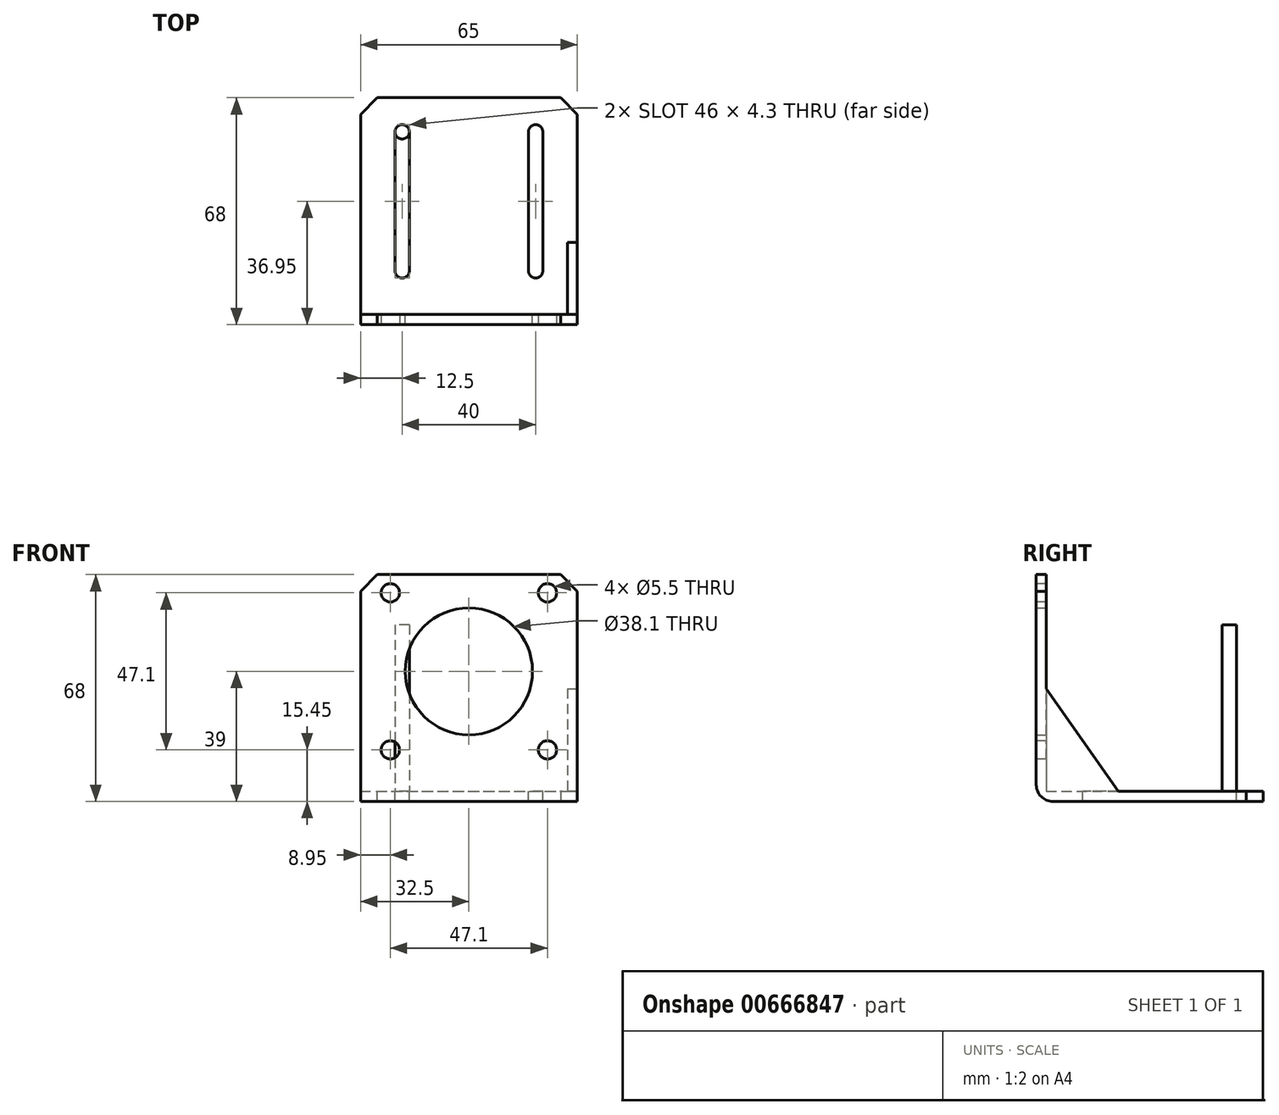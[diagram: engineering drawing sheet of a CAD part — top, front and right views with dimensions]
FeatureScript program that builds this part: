
annotation { "Feature Type Name" : "Feature", "Feature Type Description" : "" }
export const myFeature = defineFeature(function(context is Context, id is Id, definition is map)
    precondition{}
    {
        {
            var Q0;
            Q0=qCreatedBy(makeId("Top.planeOp"),FACE);
            var sketch = newSketch(context, id + "F0", { "sketchPlane" : qUnion([Q0])});
            skLineSegment(sketch, "E0.bottom", {"start": v(0, 0) * mm, "end": v(65, 0) * mm});
            skLineSegment(sketch, "E0.top", {"start": v(0, 65) * mm, "end": v(65, 65) * mm});
            skLineSegment(sketch, "E0.left", {"start": v(0, 0) * mm, "end": v(0, 65) * mm});
            skLineSegment(sketch, "E0.right", {"start": v(65, 0) * mm, "end": v(65, 65) * mm});
            skLineSegment(sketch, "E1.top", {"start": v(0, -3) * mm, "end": v(65, -3) * mm});
            skLineSegment(sketch, "E1.left", {"start": v(0, 0) * mm, "end": v(0, -3) * mm});
            skLineSegment(sketch, "E1.right", {"start": v(65, 0) * mm, "end": v(65, -3) * mm});
            skSolve(sketch);
        }
        {
            var Q0;
            Q0=makeQuery(id+"F0.imprint","IMPRINT",FACE,{"disambiguationData":[TD([[makeQuery(id+"F0.imprint","IMPRINT",EDGE,{"derivedFrom":sQuery(id+"F0.wireOp",EDGE,"E0.top")}),-1.0]])]});
            extrude(context, id + "F1", {"entities" : qUnion([Q0]), "depth" : 3 * mm, "offsetDistance" : 25 * mm});
        }
        {
            var Q0;
            Q0=makeQuery(id+"F0.imprint","IMPRINT",FACE,{"disambiguationData":[TD([[makeQuery(id+"F0.imprint","IMPRINT",EDGE,{"derivedFrom":sQuery(id+"F0.wireOp",EDGE,"E0.bottom")}),-1.0]])]});
            extrude(context, id + "F2", {"entities" : qUnion([Q0]), "operationType" : NewBodyOperationType.ADD, "depth" : 68 * mm, "offsetDistance" : 25 * mm});
        }
        {
            var Q0;
            Q0=makeQuery(id+"F2.opExtrude","CAP_EDGE",EDGE,{"disambiguationData":[OSD([sQuery(id+"F0.wireOp",EDGE,"E1.top")])],"isStart":true});
            fillet(context, id + "F3", {"entities" : qUnion([Q0]), "radius" : 5 * mm, "tangentPropagation" : true, "allowEdgeOverflow" : false});
        }
        {
            var Q0;
            Q0=makeQuery(id+"F2.opExtrude","CAP_EDGE",EDGE,{"disambiguationData":[OSD([sQuery(id+"F0.wireOp",EDGE,"E1.right")])],"isStart":false});
            var Q1;
            Q1=makeQuery(id+"F2.opExtrude","CAP_EDGE",EDGE,{"disambiguationData":[OSD([sQuery(id+"F0.wireOp",EDGE,"E1.left")])],"isStart":false});
            chamfer(context, id + "F4", {"entities" : qUnion([Q0, Q1]), "width" : 5 * mm, "tangentPropagation" : true});
        }
        {
            var Q0;
            Q0=makeQuery(id+"F2.opExtrude","SWEPT_FACE",FACE,{"disambiguationData":[OSD([sQuery(id+"F0.wireOp",EDGE,"E0.bottom")])]});
            var sketch = newSketch(context, id + "F5", { "sketchPlane" : qUnion([Q0])});
            skCircle(sketch, "E2", {"center": v(-32.5, 39) * mm, "radius": 19.05 * mm});
            skLineSegment(sketch, "E3.bottom", {"start": v(-8.95, 62.55) * mm, "end": v(-56.05, 62.55) * mm, "construction": true});
            skLineSegment(sketch, "E3.top", {"start": v(-8.95, 15.45) * mm, "end": v(-56.05, 15.45) * mm, "construction": true});
            skLineSegment(sketch, "E3.left", {"start": v(-8.95, 62.55) * mm, "end": v(-8.95, 15.45) * mm, "construction": true});
            skLineSegment(sketch, "E3.right", {"start": v(-56.05, 62.55) * mm, "end": v(-56.05, 15.45) * mm, "construction": true});
            skLineSegment(sketch, "E4", {"start": v(-32.5, 39) * mm, "end": v(-32.5, 68) * mm, "construction": true});
            skLineSegment(sketch, "E5", {"start": v(-65, 39) * mm, "end": v(-32.5, 39) * mm, "construction": true});
            skPoint(sketch, "E5.startSnap0", {"position": v(-56.05, 39) * mm});
            skLineSegment(sketch, "E6", {"start": v(-32.5, 39) * mm, "end": v(0, 39) * mm, "construction": true});
            skSolve(sketch);
        }
        {
            var Q0;
            Q0=sQuery(id+"F5.wireOp",VERTEX,"E3.bottom.end");
            var Q1;
            Q1=sQuery(id+"F5.wireOp",VERTEX,"E3.bottom.start");
            var Q2;
            Q2=sQuery(id+"F5.wireOp",VERTEX,"E3.top.start");
            var Q3;
            Q3=sQuery(id+"F5.wireOp",VERTEX,"E3.top.end");
            var Q4;
            Q4=makeQuery(id+"F1.opExtrude","SWEPT_BODY",BODY,{"disambiguationData":[OSD([sQuery(id+"F0.wireOp",EDGE,"E0.top"),sQuery(id+"F0.wireOp",EDGE,"E0.left"),sQuery(id+"F0.wireOp",EDGE,"E0.right"),sQuery(id+"F0.wireOp",EDGE,"E0.bottom")])]});
            hole(context, id + "F6", {"style" : HoleStyle.SIMPLE, "endStyle" : HoleEndStyle.THROUGH, "holeDiameter" : 5.5 * mm, "majorDiameter" : 5 * mm, "isTappedThrough" : true, "tappedDepth" : 12 * mm, "tapClearance" : 3, "locations" : qUnion([Q0, Q1, Q2, Q3]), "scope" : qUnion([Q4])});
        }
        {
            var Q0;
            Q0=makeQuery(id+"F5.imprint","IMPRINT",FACE,{"disambiguationData":[TD([[makeQuery(id+"F5.imprint","IMPRINT",EDGE,{"derivedFrom":sQuery(id+"F5.wireOp",EDGE,"E2")}),1.0]])]});
            extrude(context, id + "F7", {"entities" : qUnion([Q0]), "operationType" : NewBodyOperationType.REMOVE, "oppositeDirection" : true, "depth" : 25 * mm, "offsetDistance" : 25 * mm});
        }
        {
            var Q0;
            Q0=makeQuery(id+"F2.boolean.opBoolean","MERGE",FACE,{"derivedFrom":[makeQuery(id+"F1.opExtrude","SWEPT_FACE",FACE,{"disambiguationData":[OSD([sQuery(id+"F0.wireOp",EDGE,"E0.right")])]}),makeQuery(id+"F2.opExtrude","SWEPT_FACE",FACE,{"disambiguationData":[OSD([sQuery(id+"F0.wireOp",EDGE,"E1.right")])]})]});
            var sketch = newSketch(context, id + "F8", { "sketchPlane" : qUnion([Q0])});
            skLineSegment(sketch, "E7", {"start": v(0, 33.83) * mm, "end": v(21.59, 3) * mm});
            skSolve(sketch);
        }
        {
            var Q0;
            Q0 = qSketchRegion(id + "F8", true);
            var Q1;
            {var subQ0=sQuery(id+"F8.wireOp",EDGE,"E7");Q1=makeQuery(id+"F8.imprint","IMPRINT",FACE,{"disambiguationData":[TD([[makeQuery(id+"F8.imprint","IMPRINT",EDGE,{"derivedFrom":subQ0}),-1.0]])]});}
            extrude(context, id + "F9", {"entities" : qUnion([Q0, Q1]), "operationType" : NewBodyOperationType.ADD, "oppositeDirection" : true, "depth" : 3 * mm, "offsetDistance" : 25 * mm});
        }
        {
            var Q0;
            Q0=makeQuery(id+"F1.opExtrude","SWEPT_EDGE",EDGE,{"disambiguationData":[OSD([sQuery(id+"F0.wireOp",EDGE,"E0.top"),sQuery(id+"F0.wireOp",EDGE,"E0.right")])]});
            var Q1;
            Q1=makeQuery(id+"F1.opExtrude","SWEPT_EDGE",EDGE,{"disambiguationData":[OSD([sQuery(id+"F0.wireOp",EDGE,"E0.top"),sQuery(id+"F0.wireOp",EDGE,"E0.left")])]});
            chamfer(context, id + "F10", {"entities" : qUnion([Q0, Q1]), "width" : 5 * mm, "tangentPropagation" : true});
        }
        {
            var Q0;
            Q0=makeQuery(id+"F1.opExtrude","CAP_FACE",FACE,{"disambiguationData":[OSD([sQuery(id+"F0.wireOp",EDGE,"E0.top"),sQuery(id+"F0.wireOp",EDGE,"E0.left"),sQuery(id+"F0.wireOp",EDGE,"E0.right"),sQuery(id+"F0.wireOp",EDGE,"E0.bottom")])],"isStart":false});
            var sketch = newSketch(context, id + "F11", { "sketchPlane" : qUnion([Q0])});
            skLineSegment(sketch, "E8", {"start": v(32.5, 65) * mm, "end": v(32.5, 54.8) * mm, "construction": true});
            skLineSegment(sketch, "E9", {"start": v(32.5, 54.8) * mm, "end": v(52.5, 54.8) * mm});
            skLineSegment(sketch, "E10", {"start": v(32.5, 54.8) * mm, "end": v(12.5, 54.8) * mm});
            skCircle(sketch, "E11", {"center": v(12.5, 54.8) * mm, "radius": 2.15 * mm});
            skCircle(sketch, "E12", {"center": v(52.5, 54.8) * mm, "radius": 2.15 * mm});
            skLineSegment(sketch, "E13", {"start": v(12.5, 54.8) * mm, "end": v(12.5, 13.1) * mm, "construction": true});
            skLineSegment(sketch, "E14", {"start": v(52.5, 54.8) * mm, "end": v(52.5, 13.1) * mm, "construction": true});
            skCircle(sketch, "E15", {"center": v(12.5, 13.1) * mm, "radius": 2.15 * mm});
            skCircle(sketch, "E16", {"center": v(52.5, 13.1) * mm, "radius": 2.15 * mm});
            skLineSegment(sketch, "E17", {"start": v(10.35, 54.8) * mm, "end": v(10.35, 13.1) * mm});
            skLineSegment(sketch, "E18", {"start": v(14.65, 54.8) * mm, "end": v(14.65, 13.1) * mm});
            skLineSegment(sketch, "E19", {"start": v(50.35, 54.8) * mm, "end": v(50.35, 13.1) * mm});
            skLineSegment(sketch, "E20", {"start": v(54.65, 54.8) * mm, "end": v(54.65, 13.1) * mm});
            skSolve(sketch);
        }
        {
            var Q0;
            {var subQ0=sQuery(id+"F11.wireOp",EDGE,"E17");Q0=makeQuery(id+"F11.imprint","IMPRINT",FACE,{"disambiguationData":[TD([[makeQuery(id+"F11.imprint","IMPRINT",EDGE,{"derivedFrom":subQ0}),1.0]])]});}
            var Q1;
            {var subQ0=sQuery(id+"F11.wireOp",EDGE,"E19");Q1=makeQuery(id+"F11.imprint","IMPRINT",FACE,{"disambiguationData":[TD([[makeQuery(id+"F11.imprint","IMPRINT",EDGE,{"derivedFrom":subQ0}),1.0]])]});}
            var Q2;
            {var subQ0=sQuery(id+"F11.wireOp",EDGE,"E16");var subQ1=makeQuery(id+"F11.imprint","INTERSECT",VERTEX,{"derivedFrom":[subQ0,sQuery(id+"F11.wireOp",EDGE,"E19")]});Q2=makeQuery(id+"F11.imprint","IMPRINT",FACE,{"disambiguationData":[TD([[makeQuery(id+"F11.imprint","IMPRINT",EDGE,{"disambiguationData":[TD([[subQ1,1.0]])],"derivedFrom":subQ0}),1.0]])]});}
            var Q3;
            {var subQ0=sQuery(id+"F11.wireOp",EDGE,"E15");var subQ1=makeQuery(id+"F11.imprint","INTERSECT",VERTEX,{"derivedFrom":[subQ0,sQuery(id+"F11.wireOp",EDGE,"E17")]});Q3=makeQuery(id+"F11.imprint","IMPRINT",FACE,{"disambiguationData":[TD([[makeQuery(id+"F11.imprint","IMPRINT",EDGE,{"disambiguationData":[TD([[subQ1,1.0]])],"derivedFrom":subQ0}),1.0]])]});}
            var Q4;
            {var subQ0=sQuery(id+"F11.wireOp",EDGE,"E12");var subQ1=makeQuery(id+"F11.imprint","INTERSECT",VERTEX,{"derivedFrom":[subQ0,sQuery(id+"F11.wireOp",EDGE,"E19")]});Q4=makeQuery(id+"F11.imprint","IMPRINT",FACE,{"disambiguationData":[TD([[makeQuery(id+"F11.imprint","IMPRINT",EDGE,{"disambiguationData":[TD([[subQ1,1.0]])],"derivedFrom":subQ0}),1.0]])]});}
            var Q5;
            {var subQ0=sQuery(id+"F11.wireOp",EDGE,"E11");var subQ1=makeQuery(id+"F11.imprint","INTERSECT",VERTEX,{"derivedFrom":[subQ0,sQuery(id+"F11.wireOp",EDGE,"E17")]});Q5=makeQuery(id+"F11.imprint","IMPRINT",FACE,{"disambiguationData":[TD([[makeQuery(id+"F11.imprint","IMPRINT",EDGE,{"disambiguationData":[TD([[subQ1,1.0]])],"derivedFrom":subQ0}),1.0]])]});}
            extrude(context, id + "F12", {"entities" : qUnion([Q0, Q1, Q2, Q3, Q4, Q5]), "operationType" : NewBodyOperationType.REMOVE, "oppositeDirection" : true, "depth" : 25 * mm, "offsetDistance" : 25 * mm});
        }
        {
            var Q0;
            {var subQ0=sQuery(id+"F11.wireOp",EDGE,"E11");var subQ1=makeQuery(id+"F11.imprint","INTERSECT",VERTEX,{"derivedFrom":[subQ0,sQuery(id+"F11.wireOp",EDGE,"E17")]});Q0=makeQuery(id+"F11.imprint","IMPRINT",FACE,{"disambiguationData":[TD([[makeQuery(id+"F11.imprint","IMPRINT",EDGE,{"disambiguationData":[TD([[subQ1,1.0]])],"derivedFrom":subQ0}),1.0]])]});}
            extrude(context, id + "F13", {"entities" : qUnion([Q0]), "depth" : 50 * mm, "offsetDistance" : 25 * mm});
        }
    });
